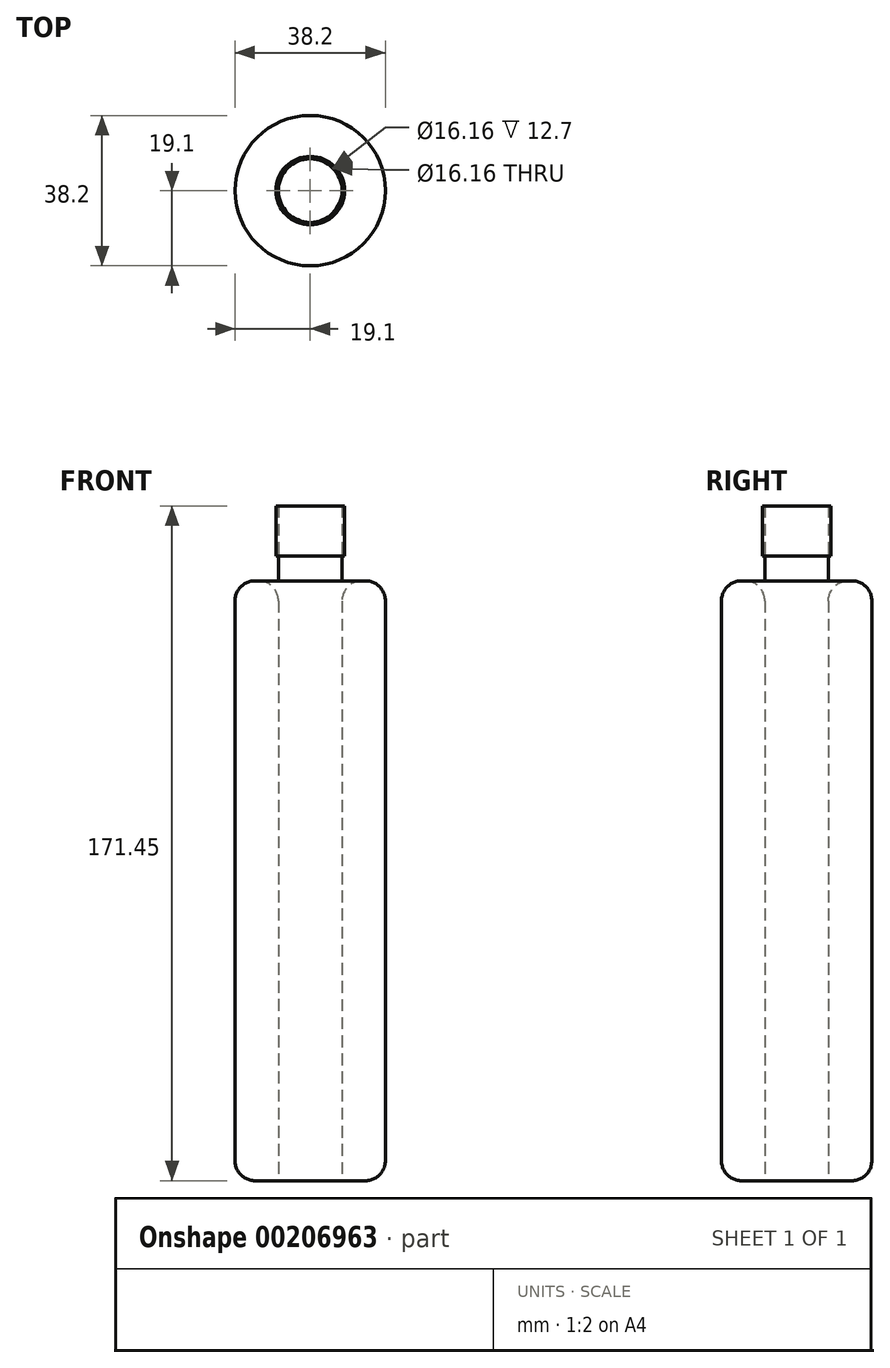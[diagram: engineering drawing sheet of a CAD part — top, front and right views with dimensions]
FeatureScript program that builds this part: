
annotation { "Feature Type Name" : "Feature", "Feature Type Description" : "" }
export const myFeature = defineFeature(function(context is Context, id is Id, definition is map)
    precondition{}
    {
        {
            var Q0;
            Q0=qCreatedBy(makeId("Top.planeOp"),FACE);
            var sketch = newSketch(context, id + "F0", { "sketchPlane" : qUnion([Q0])});
            skCircle(sketch, "E0", {"center": v(0, 0) * mm, "radius": 8.08 * mm});
            skCircle(sketch, "E1", {"center": v(0, 0) * mm, "radius": 19.1 * mm});
            skSolve(sketch);
        }
        {
            var Q0;
            Q0=makeQuery(id+"F0.imprint","IMPRINT",FACE,{"disambiguationData":[TD([[makeQuery(id+"F0.imprint","IMPRINT",EDGE,{"derivedFrom":sQuery(id+"F0.wireOp",EDGE,"E0")}),-1.0]])]});
            extrude(context, id + "F1", {"entities" : qUnion([Q0]), "endBound" : BoundingType.SYMMETRIC, "depth" : 152.4 * mm});
        }
        {
            var Q0;
            Q0=makeQuery(id+"F1.opExtrude","CAP_FACE",FACE,{"disambiguationData":[OSD([sQuery(id+"F0.wireOp",EDGE,"E0"),sQuery(id+"F0.wireOp",EDGE,"E1")])],"isStart":false});
            var sketch = newSketch(context, id + "F2", { "sketchPlane" : qUnion([Q0])});
            skCircle(sketch, "E2", {"center": v(0, 0) * mm, "radius": 8.54 * mm});
            skSolve(sketch);
        }
        {
            var Q0;
            Q0=makeQuery(id+"F1.opExtrude","CAP_EDGE",EDGE,{"disambiguationData":[OSD([sQuery(id+"F0.wireOp",EDGE,"E1")])],"isStart":true});
            fillet(context, id + "F3", {"entities" : qUnion([Q0]), "radius" : 5.08 * mm, "tangentPropagation" : true, "allowEdgeOverflow" : false});
        }
        {
            var Q0;
            Q0=makeQuery(id+"F2.imprint","IMPRINT",FACE,{"disambiguationData":[TD([[makeQuery(id+"F2.imprint","IMPRINT",EDGE,{"derivedFrom":makeQuery(id+"F1.opExtrude","CAP_EDGE",EDGE,{"disambiguationData":[OSD([sQuery(id+"F0.wireOp",EDGE,"E0")])],"isStart":false})}),1.0]])]});
            extrude(context, id + "F4", {"entities" : qUnion([Q0]), "depth" : 6.35 * mm});
        }
        {
            var Q0;
            Q0=makeQuery(id+"F4.opExtrude","CAP_FACE",FACE,{"disambiguationData":[OSD([sQuery(id+"F0.wireOp",EDGE,"E0")])],"isStart":false});
            var sketch = newSketch(context, id + "F5", { "sketchPlane" : qUnion([Q0])});
            skCircle(sketch, "E3", {"center": v(0, 0) * mm, "radius": 8.09 * mm});
            skSolve(sketch);
        }
        {
            var Q0;
            Q0=makeQuery(id+"F2VP6gyjvsRE8lu_2.opExtrude","CAP_EDGE",EDGE,{"disambiguationData":[OSD([sQuery(id+"F5.wireOp",EDGE,"E3")])],"isStart":true});
            var Q1;
            Q1=makeQuery(id+"F1.opExtrude","CAP_FACE",FACE,{"disambiguationData":[OSD([sQuery(id+"F0.wireOp",EDGE,"E0"),sQuery(id+"F0.wireOp",EDGE,"E1")])],"isStart":false});
            fillet(context, id + "F6", {"entities" : qUnion([Q0, Q1]), "radius" : 5.08 * mm, "tangentPropagation" : true, "allowEdgeOverflow" : false});
        }
        {
            var Q0;
            Q0=makeQuery(id+"F5.imprint","IMPRINT",FACE,{"disambiguationData":[TD([[makeQuery(id+"F5.imprint","IMPRINT",EDGE,{"derivedFrom":makeQuery(id+"F4.opExtrude","CAP_EDGE",EDGE,{"disambiguationData":[OSD([sQuery(id+"F0.wireOp",EDGE,"E0")])],"isStart":false})}),1.0]])]});
            var sketch = newSketch(context, id + "F7", { "sketchPlane" : qUnion([Q0])});
            skCircle(sketch, "E4", {"center": v(0, 0) * mm, "radius": 8.72 * mm});
            skSolve(sketch);
        }
        {
            var Q0;
            Q0=makeQuery(id+"F7.imprint","IMPRINT",FACE,{"disambiguationData":[TD([[makeQuery(id+"F7.imprint","IMPRINT",EDGE,{"derivedFrom":sQuery(id+"F7.wireOp",EDGE,"E4")}),1.0]])]});
            extrude(context, id + "F8", {"entities" : qUnion([Q0]), "depth" : 12.7 * mm});
        }
    });
